# Revit family: LWplc_Latchwaysplc_FallArrestSystemGuidedAnchorLine_EndSet
name_source: partatom
category: Generic Models
revit_build: Autodesk Revit 2014 (Build: 20130709_2115(x64)
units: mm (PartAtom-declared; Revit-internal decimal feet)

## types (1)
- ManSafe CFP - End Set
    AssetType = Fixed
    AttachmentDeviceGuide = www.latchways.com/BIM/Latchways_Attachment_Device_Guide.pdf
    BIMObjectName = LWplc_Latchwaysplc_FallArrestSystemGuidedAnchorLine_EndSet
    Default Elevation = 1219 mm
    Description = Latchways ManSafe® for Roofing, using Constant Force posts
    DurationUnit = year
    FireExit = No
    IfcExportAs = NOTDEFINED
    IfcExportType = IfcTransportElement
    ManSafeForRoofingBrochure = www.latchways.com/BIM/MansafeForRoofing.pdf
    ManufacturerName = Latchways plc
    ManufacturerURL = www.latchways.com
    ModelReference = Constant Force Post  - End Set
    NBSDescription = Fall arrest system - guided anchor line
    NBSReference = 80-50-25/110
    Name = FallArrestSystemGuidedAnchorLine_EndSet_Latchwaysplc
    NominalHeight = 49 mm
    NominalLength = 215 mm
    NominalWidth = 36 mm  [stored 0.11811 ft]
    PreInstallationSurvey = Required
    ProductInformation = www.latchways.com/BIM/Latchways_ConstantForcePost_EndSet_TopComponents.pdf
    ProductSpecification = www.latchways.com/BIM/Latchways_Specification_ConstantForcePost.pdf
    Size = 36 x 215 x 49 mm
    SystemMaintenance = Annual service to be completed by Latchways registered installers in accordance with BS7883:2005
    SystemManufacturer = Latchways plc
    URL = www.latchways.com
    Uniclass2 = 80-30-25/135
    Version = 1
    WarrantyDurationUnit = year

note: [stored X ft] marks values corroborated as IEEE doubles in the binary element streams (Revit-internal decimal feet)

## geometry (parser evidence)
native form markers: Sweep x5
no freeform markers — native parametric forms only
